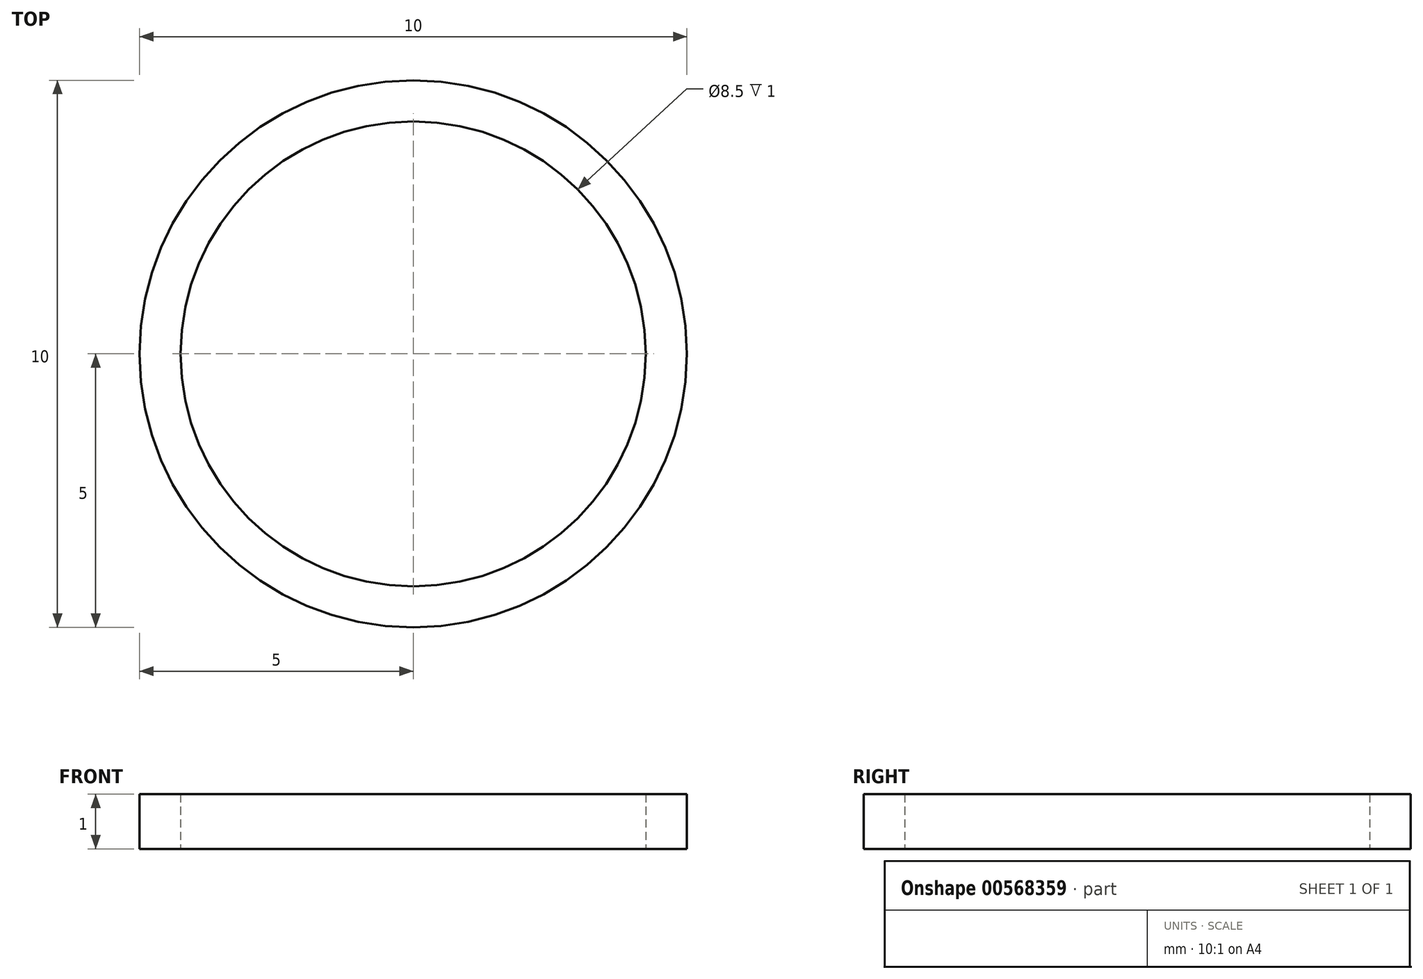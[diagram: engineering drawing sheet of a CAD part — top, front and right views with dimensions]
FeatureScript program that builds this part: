
annotation { "Feature Type Name" : "Feature", "Feature Type Description" : "" }
export const myFeature = defineFeature(function(context is Context, id is Id, definition is map)
    precondition{}
    {
        {
            var Q0;
            Q0=qCreatedBy(makeId("Top.planeOp"),FACE);
            var sketch = newSketch(context, id + "F0", { "sketchPlane" : qUnion([Q0])});
            skCircle(sketch, "E0", {"center": v(0, 0) * mm, "radius": 5 * mm});
            skCircle(sketch, "E1", {"center": v(0, 0) * mm, "radius": 4.25 * mm});
            skSolve(sketch);
        }
        {
            var Q0;
            Q0=makeQuery(id+"F0.imprint","IMPRINT",FACE,{"disambiguationData":[TD([[makeQuery(id+"F0.imprint","IMPRINT",EDGE,{"derivedFrom":sQuery(id+"F0.wireOp",EDGE,"E0")}),1.0]])]});
            extrude(context, id + "F1", {"entities" : qUnion([Q0]), "depth" : 1 * mm, "offsetDistance" : 25 * mm});
        }
    });
